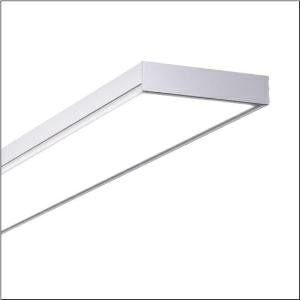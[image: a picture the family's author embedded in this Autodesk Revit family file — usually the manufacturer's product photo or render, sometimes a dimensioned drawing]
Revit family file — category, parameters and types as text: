
# Revit family: apollon_r__31_surface_51mp25wm2341e_e42f
name_source: partatom
category: Lighting Fixtures
units: mm (PartAtom-declared; Revit-internal decimal feet)

## family parameters
Cut with Voids When Loaded = No
Host = Face
Light Source = No
Part Type = Normal
Room Calculation Point = No
Round Connector Dimension = Use Diameter
Shared = No

## types (1)
- Apollon® 31 Surface (1 x LED, 3600 lm, 27 W, 3000K)
    Apparent Load = 27 VA
    CIE Flux Codes = 61 87 97 97 100
    Color Rendering = 80
    Color Temperature = 3000K
    Default Elevation = 1800 mm
    Description = Apollon® 31 Surface, office luminaire, primary optical cover: micro prismatic cover, of PMMA, light emission: direct distribution, primary light characteristic: symmetric, installation type: surface-mounted, LED, rated luminous flux: 3.600lm, luminous efficacy: 132lm/W, light colour: 830, colour temperature: 3000K, control gear: ECG Multilumen, with terminal, 3-pole, mains connection: 220..240V, AC, 50/60Hz, rated input power: 27W, housing, of sheet steel, coil coated, metallic grey (RAL 9006), length: 1.245mm, width: 200mm, height: 44mm, protection rating (complete): IP20, insulation class (complete): insulation class II (safety insulation), certification: CE, impact resistance: IK02, permissible operating ambient temperature: -20..+40°C, packaging unit: 1 piece
    Height = 44 mm
    Lamp = 1 x LED
    Lamp Light Flux = 3600 lm
    Lamp Power = 27 W
    Lamp count = 1
    Length = 1245 mm
    Luminous efficacy = 133 lm/W
    Manufacturer = Siteco
    ModVariant = No
    Model = 51MP25WM2341E
    Mounting Place = Ceiling
    Mounting Type = Surface mounted
    Number of Poles = 1
    OnlyDefault = Yes
    Power Factor = 1
    Product Name = Apollon® 31 Surface
    Product group = office luminaire | ceiling mounted
    ProductGroupID = 304
    Protection Class = Protection class II
    Protection Degree = IP 20
    RLX_Detail_Level = 1
    RLX_Emergency_Light_Flux = 0 lm
    RLX_Emergency_Type = 0
    RLX_Emergency_Type_DB = No
    RlxData = <blob elided: 24081 chars, md5=c9968bb2>
    Socket = socket
    Standby Power = 0 W
    System Light Flux = 3600 lm
    System Power = 27 W
    Type Comments = Product without accessories
    Type Image = l_1007091.jpg
    URL = http://relux.com
    VarID = ---
    Voltage = 0 V
    Weight = 0.00 kg
    Width = 200 mm  [stored 0.656168 ft]

note: [stored X ft] marks values corroborated as IEEE doubles in the binary element streams (Revit-internal decimal feet)

## geometry (parser evidence)
native form markers: Blend x4, Sweep x9
no freeform markers — native parametric forms only
